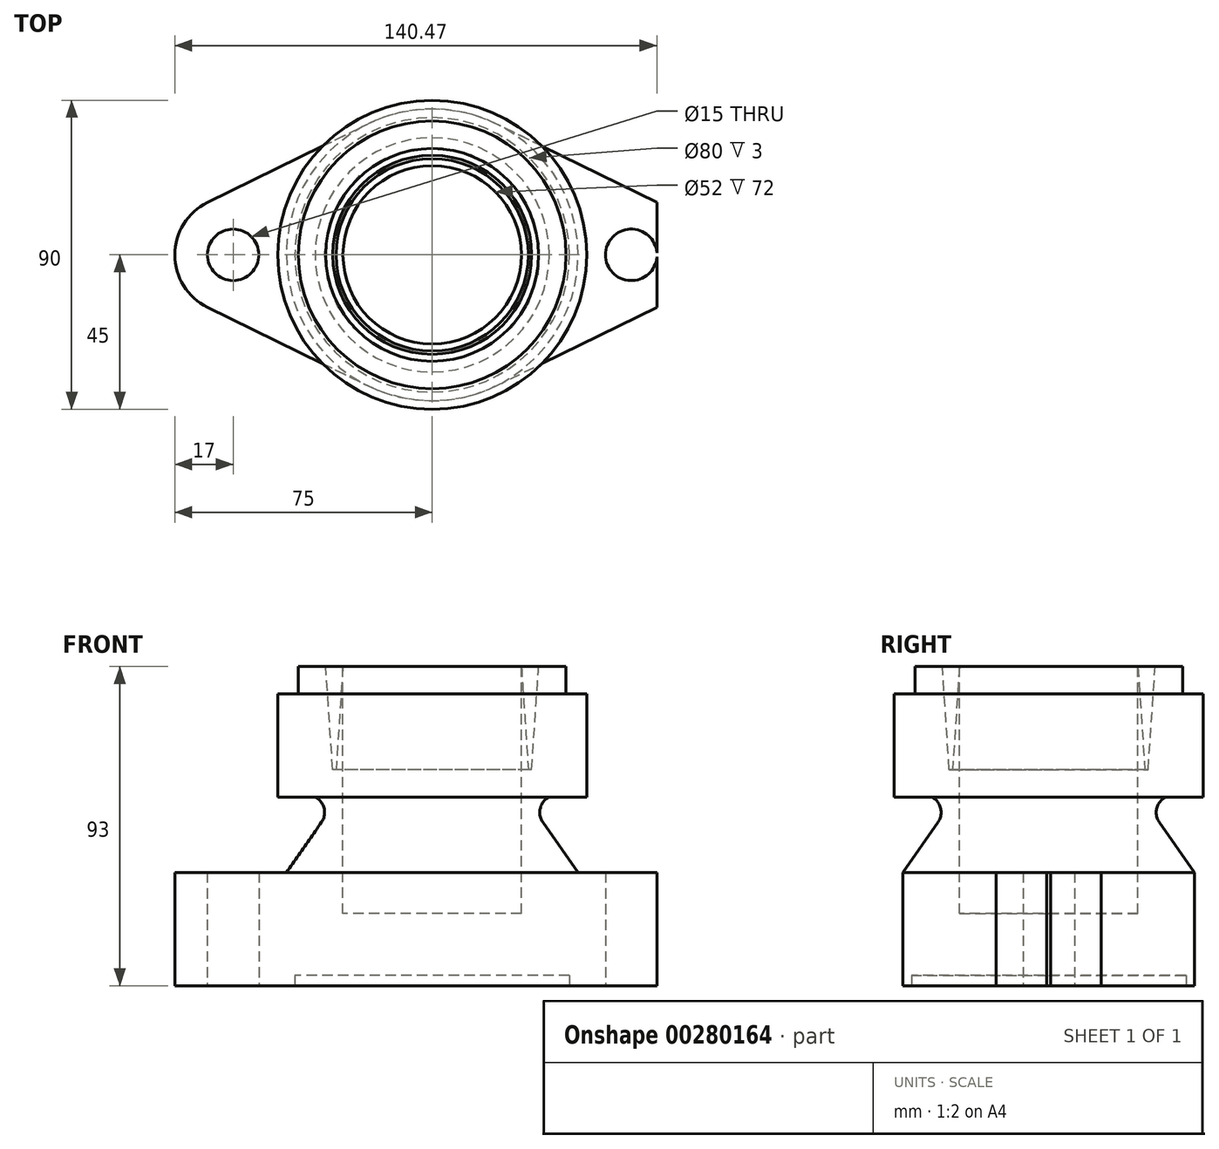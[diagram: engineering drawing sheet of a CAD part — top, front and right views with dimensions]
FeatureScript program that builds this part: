
annotation { "Feature Type Name" : "Feature", "Feature Type Description" : "" }
export const myFeature = defineFeature(function(context is Context, id is Id, definition is map)
    precondition{}
    {
        {
            var Q0;
            Q0=qCreatedBy(makeId("Top.planeOp"),FACE);
            var sketch = newSketch(context, id + "F0", { "sketchPlane" : qUnion([Q0])});
            skCircle(sketch, "E0", {"center": v(0, 0) * mm, "radius": 42.5 * mm});
            skCircle(sketch, "E1", {"center": v(-58, 0) * mm, "radius": 7.5 * mm});
            skCircle(sketch, "E2", {"center": v(58, 0) * mm, "radius": 7.5 * mm});
            skCircle(sketch, "E3", {"center": v(-58, 0) * mm, "radius": 17 * mm});
            skCircle(sketch, "E4", {"center": v(58, 0) * mm, "radius": 17 * mm});
            skLineSegment(sketch, "E5", {"start": v(-65.47, -15.27) * mm, "end": v(-18.69, -38.17) * mm});
            skLineSegment(sketch, "E6", {"start": v(-65.47, 15.27) * mm, "end": v(-18.69, 38.17) * mm});
            skLineSegment(sketch, "E7", {"start": v(65.47, 15.27) * mm, "end": v(18.69, 38.17) * mm});
            skLineSegment(sketch, "E8", {"start": v(18.69, -38.17) * mm, "end": v(65.47, -15.27) * mm});
            skLineSegment(sketch, "E9", {"start": v(-65.47, -15.27) * mm, "end": v(-65.47, 15.27) * mm});
            skLineSegment(sketch, "E10", {"start": v(65.47, -15.27) * mm, "end": v(65.47, 15.27) * mm});
            skPoint(sketch, "E11.orphan", {"position": v(-58, 17) * mm});
            skSolve(sketch);
        }
        {
            var Q0;
            {var subQ0=sQuery(id+"F0.wireOp",EDGE,"E9");var subQ1=sQuery(id+"F0.wireOp",EDGE,"E1");var subQ2=makeQuery(id+"F0.imprint","INTERSECT",VERTEX,{"disambiguationData":[OD(0.0)],"derivedFrom":[subQ1,subQ0]});Q0=makeQuery(id+"F0.imprint","IMPRINT",FACE,{"disambiguationData":[TD([[makeQuery(id+"F0.imprint","IMPRINT",EDGE,{"disambiguationData":[TD([[subQ2,1.0]])],"derivedFrom":subQ1}),-1.0]])]});}
            var Q1;
            {var subQ0=sQuery(id+"F0.wireOp",EDGE,"E5");Q1=makeQuery(id+"F0.imprint","IMPRINT",FACE,{"disambiguationData":[TD([[makeQuery(id+"F0.imprint","IMPRINT",EDGE,{"derivedFrom":subQ0}),1.0]])]});}
            var Q2;
            {var subQ0=sQuery(id+"F0.wireOp",EDGE,"E9");var subQ1=sQuery(id+"F0.wireOp",EDGE,"E1");var subQ2=makeQuery(id+"F0.imprint","INTERSECT",VERTEX,{"disambiguationData":[OD(0.0)],"derivedFrom":[subQ1,subQ0]});Q2=makeQuery(id+"F0.imprint","IMPRINT",FACE,{"disambiguationData":[TD([[makeQuery(id+"F0.imprint","IMPRINT",EDGE,{"disambiguationData":[TD([[subQ2,-1.0]])],"derivedFrom":subQ1}),-1.0]])]});}
            var Q3;
            {var subQ0=sQuery(id+"F0.wireOp",EDGE,"E7");Q3=makeQuery(id+"F0.imprint","IMPRINT",FACE,{"disambiguationData":[TD([[makeQuery(id+"F0.imprint","IMPRINT",EDGE,{"derivedFrom":subQ0}),1.0]])]});}
            var Q4;
            {var subQ0=sQuery(id+"F0.wireOp",EDGE,"E10");var subQ1=sQuery(id+"F0.wireOp",EDGE,"E2");var subQ2=makeQuery(id+"F0.imprint","INTERSECT",VERTEX,{"disambiguationData":[OD(0.0)],"derivedFrom":[subQ1,subQ0]});Q4=makeQuery(id+"F0.imprint","IMPRINT",FACE,{"disambiguationData":[TD([[makeQuery(id+"F0.imprint","IMPRINT",EDGE,{"disambiguationData":[TD([[subQ2,-1.0]])],"derivedFrom":subQ1}),-1.0]])]});}
            var Q5;
            {var subQ0=sQuery(id+"F0.wireOp",EDGE,"E0");var subQ1=makeQuery(id+"F0.imprint","INTERSECT",VERTEX,{"derivedFrom":[subQ0,sQuery(id+"F0.wireOp",EDGE,"E6")]});Q5=makeQuery(id+"F0.imprint","IMPRINT",FACE,{"disambiguationData":[TD([[makeQuery(id+"F0.imprint","IMPRINT",EDGE,{"disambiguationData":[TD([[subQ1,1.0]])],"derivedFrom":subQ0}),1.0]])]});}
            var Q6;
            {var subQ0=sQuery(id+"F0.wireOp",EDGE,"E4");var subQ1=sQuery(id+"F0.wireOp",EDGE,"E0");var subQ2=makeQuery(id+"F0.imprint","INTERSECT",VERTEX,{"disambiguationData":[OD(0.0)],"derivedFrom":[subQ1,subQ0]});Q6=makeQuery(id+"F0.imprint","IMPRINT",FACE,{"disambiguationData":[TD([[makeQuery(id+"F0.imprint","IMPRINT",EDGE,{"disambiguationData":[TD([[subQ2,1.0]])],"derivedFrom":subQ1}),1.0]])]});}
            var Q7;
            {var subQ1=sQuery(id+"F0.wireOp",EDGE,"E4");var subQ3=sQuery(id+"F0.wireOp",EDGE,"E0");var subQ5=makeQuery(id+"F0.imprint","INTERSECT",VERTEX,{"disambiguationData":[OD(0.0)],"derivedFrom":[subQ3,subQ1]});Q7=makeQuery(id+"F0.imprint","IMPRINT",FACE,{"disambiguationData":[TD([[makeQuery(id+"F0.imprint","IMPRINT",EDGE,{"disambiguationData":[TD([[subQ5,1.0]])],"derivedFrom":subQ3}),-1.0]])]});}
            var Q8;
            {var subQ0=sQuery(id+"F0.wireOp",EDGE,"E8");Q8=makeQuery(id+"F0.imprint","IMPRINT",FACE,{"disambiguationData":[TD([[makeQuery(id+"F0.imprint","IMPRINT",EDGE,{"derivedFrom":subQ0}),1.0]])]});}
            var Q9;
            {var subQ0=sQuery(id+"F0.wireOp",EDGE,"E6");Q9=makeQuery(id+"F0.imprint","IMPRINT",FACE,{"disambiguationData":[TD([[makeQuery(id+"F0.imprint","IMPRINT",EDGE,{"derivedFrom":subQ0}),-1.0]])]});}
            var Q10;
            {var subQ0=sQuery(id+"F0.wireOp",EDGE,"E3");var subQ1=sQuery(id+"F0.wireOp",EDGE,"E0");var subQ2=makeQuery(id+"F0.imprint","INTERSECT",VERTEX,{"disambiguationData":[OD(0.0)],"derivedFrom":[subQ1,subQ0]});Q10=makeQuery(id+"F0.imprint","IMPRINT",FACE,{"disambiguationData":[TD([[makeQuery(id+"F0.imprint","IMPRINT",EDGE,{"disambiguationData":[TD([[subQ2,-1.0]])],"derivedFrom":subQ1}),1.0]])]});}
            extrude(context, id + "F1", {"entities" : qUnion([Q0, Q1, Q2, Q3, Q4, Q5, Q6, Q7, Q8, Q9, Q10]), "depth" : 33 * mm});
        }
        {
            var Q0;
            Q0=qCreatedBy(makeId("Front.planeOp"),FACE);
            var sketch = newSketch(context, id + "F2", { "sketchPlane" : qUnion([Q0])});
            skLineSegment(sketch, "E12", {"start": v(0, 33) * mm, "end": v(0, 55) * mm});
            skLineSegment(sketch, "E13", {"start": v(0, 55) * mm, "end": v(-27.08, 55) * mm});
            skLineSegment(sketch, "E14", {"start": v(-32.23, 47.64) * mm, "end": v(-42.5, 32.98) * mm});
            skLineSegment(sketch, "E15", {"start": v(-42.5, 32.98) * mm, "end": v(0, 33) * mm});
            skPoint(sketch, "E16.visualSharp", {"position": v(-27.08, 55) * mm});
            skArc(sketch, "E16.filletArc", {"start": v(-32.23, 47.64) * mm, "mid": v(-31.49, 51.76) * mm, "end": v(-34.12, 55) * mm});
            skLineSegment(sketch, "E17", {"start": v(-27.08, 55) * mm, "end": v(-34.12, 55) * mm});
            skLineSegment(sketch, "E18", {"start": v(-34.12, 55) * mm, "end": v(-43.87, 55) * mm});
            skSolve(sketch);
        }
        {
            var Q0;
            {var subQ0=sQuery(id+"F0.wireOp",EDGE,"E0");var subQ1=makeQuery(id+"F0.imprint","INTERSECT",VERTEX,{"derivedFrom":[subQ0,sQuery(id+"F0.wireOp",EDGE,"E6")]});Q0=makeQuery(id+"F0.imprint","IMPRINT",FACE,{"disambiguationData":[TD([[makeQuery(id+"F0.imprint","IMPRINT",EDGE,{"disambiguationData":[TD([[subQ1,1.0]])],"derivedFrom":subQ0}),1.0]])]});}
            var sketch = newSketch(context, id + "F3", { "sketchPlane" : qUnion([Q0])});
            skCircle(sketch, "E19", {"center": v(0, 0) * mm, "radius": 40 * mm});
            skSolve(sketch);
        }
        {
            var Q0;
            Q0=qSketchRegion(id+"F3",true);
            extrude(context, id + "F4", {"entities" : qUnion([Q0]), "operationType" : NewBodyOperationType.REMOVE, "depth" : 3 * mm});
        }
        {
            var Q0;
            Q0=makeQuery(id+"F2.imprint","IMPRINT",FACE,{"disambiguationData":[TD([[makeQuery(id+"F2.imprint","IMPRINT",EDGE,{"derivedFrom":sQuery(id+"F2.wireOp",EDGE,"E12")}),1.0]])]});
            var Q1;
            Q1=sQuery(id+"F2.wireOp",EDGE,"E12");
            revolve(context, id + "F5", {"operationType" : NewBodyOperationType.ADD, "entities" : qUnion([Q0]), "axis" : qUnion([Q1]), "revolveType" : RevolveType.FULL});
        }
        {
            var Q0;
            Q0=makeQuery(id+"F5.opRevolve","SWEPT_FACE",FACE,{"disambiguationData":[OSD([sQuery(id+"F2.wireOp",EDGE,"E13"),sQuery(id+"F2.wireOp",EDGE,"E17")])]});
            var sketch = newSketch(context, id + "F6", { "sketchPlane" : qUnion([Q0])});
            skCircle(sketch, "E20", {"center": v(0, 0) * mm, "radius": 45 * mm});
            skSolve(sketch);
        }
        {
            var Q0;
            Q0=makeQuery(id+"F6.imprint","IMPRINT",FACE,{"disambiguationData":[TD([[makeQuery(id+"F6.imprint","IMPRINT",EDGE,{"derivedFrom":sQuery(id+"F6.wireOp",EDGE,"E20")}),1.0]])]});
            var Q1;
            Q1=makeQuery(id+"F6.imprint","IMPRINT",FACE,{"disambiguationData":[TD([[makeQuery(id+"F6.imprint","IMPRINT",EDGE,{"derivedFrom":makeQuery(id+"F5.opRevolve","SWEPT_EDGE",EDGE,{"disambiguationData":[OSD([sQuery(id+"F2.wireOp",EDGE,"E16.filletArc"),sQuery(id+"F2.wireOp",EDGE,"E17")])]})}),-1.0]])]});
            extrude(context, id + "F7", {"entities" : qUnion([Q0, Q1]), "operationType" : NewBodyOperationType.ADD, "depth" : 38 * mm});
        }
        {
            var Q0;
            Q0=makeQuery(id+"F7.opExtrude","CAP_FACE",FACE,{"disambiguationData":[OSD([sQuery(id+"F6.wireOp",EDGE,"E20")])],"isStart":false});
            var sketch = newSketch(context, id + "F8", { "sketchPlane" : qUnion([Q0])});
            skCircle(sketch, "E21", {"center": v(0, 0) * mm, "radius": 39 * mm});
            skSolve(sketch);
        }
        {
            var Q0;
            Q0=makeQuery(id+"F8.imprint","IMPRINT",FACE,{"disambiguationData":[TD([[makeQuery(id+"F8.imprint","IMPRINT",EDGE,{"derivedFrom":sQuery(id+"F8.wireOp",EDGE,"E21")}),-1.0]])]});
            extrude(context, id + "F9", {"entities" : qUnion([Q0]), "operationType" : NewBodyOperationType.REMOVE, "oppositeDirection" : true, "depth" : 8 * mm});
        }
        {
            var Q0;
            Q0=makeQuery(id+"F7.opExtrude","CAP_FACE",FACE,{"disambiguationData":[OSD([sQuery(id+"F6.wireOp",EDGE,"E20")])],"isStart":false});
            var sketch = newSketch(context, id + "F10", { "sketchPlane" : qUnion([Q0])});
            skCircle(sketch, "E22", {"center": v(0, 0) * mm, "radius": 31 * mm});
            skSolve(sketch);
        }
        {
            var Q0;
            Q0=makeQuery(id+"F10.imprint","IMPRINT",FACE,{"disambiguationData":[TD([[makeQuery(id+"F10.imprint","IMPRINT",EDGE,{"derivedFrom":sQuery(id+"F10.wireOp",EDGE,"E22")}),1.0]])]});
            extrude(context, id + "F11", {"entities" : qUnion([Q0]), "operationType" : NewBodyOperationType.REMOVE, "oppositeDirection" : true, "depth" : 30 * mm, "hasDraft" : true, "draftAngle" : 3.85 * degree, "draftPullDirection" : true});
        }
        {
            var Q0;
            Q0=makeQuery(id+"F11.boolean.opBoolean","COPY",FACE,{"derivedFrom":makeQuery(id+"F11.opExtrude","CAP_FACE",FACE,{"disambiguationData":[OSD([sQuery(id+"F10.wireOp",EDGE,"E22")])],"isStart":false})});
            var sketch = newSketch(context, id + "F12", { "sketchPlane" : qUnion([Q0])});
            skCircle(sketch, "E23", {"center": v(0, 0) * mm, "radius": 26 * mm});
            skSolve(sketch);
        }
        {
            var Q0;
            Q0=makeQuery(id+"F12.imprint","IMPRINT",FACE,{"disambiguationData":[TD([[makeQuery(id+"F12.imprint","IMPRINT",EDGE,{"derivedFrom":sQuery(id+"F12.wireOp",EDGE,"E23")}),1.0]])]});
            extrude(context, id + "F13", {"entities" : qUnion([Q0]), "operationType" : NewBodyOperationType.REMOVE, "oppositeDirection" : true, "depth" : 42 * mm});
        }
    });
